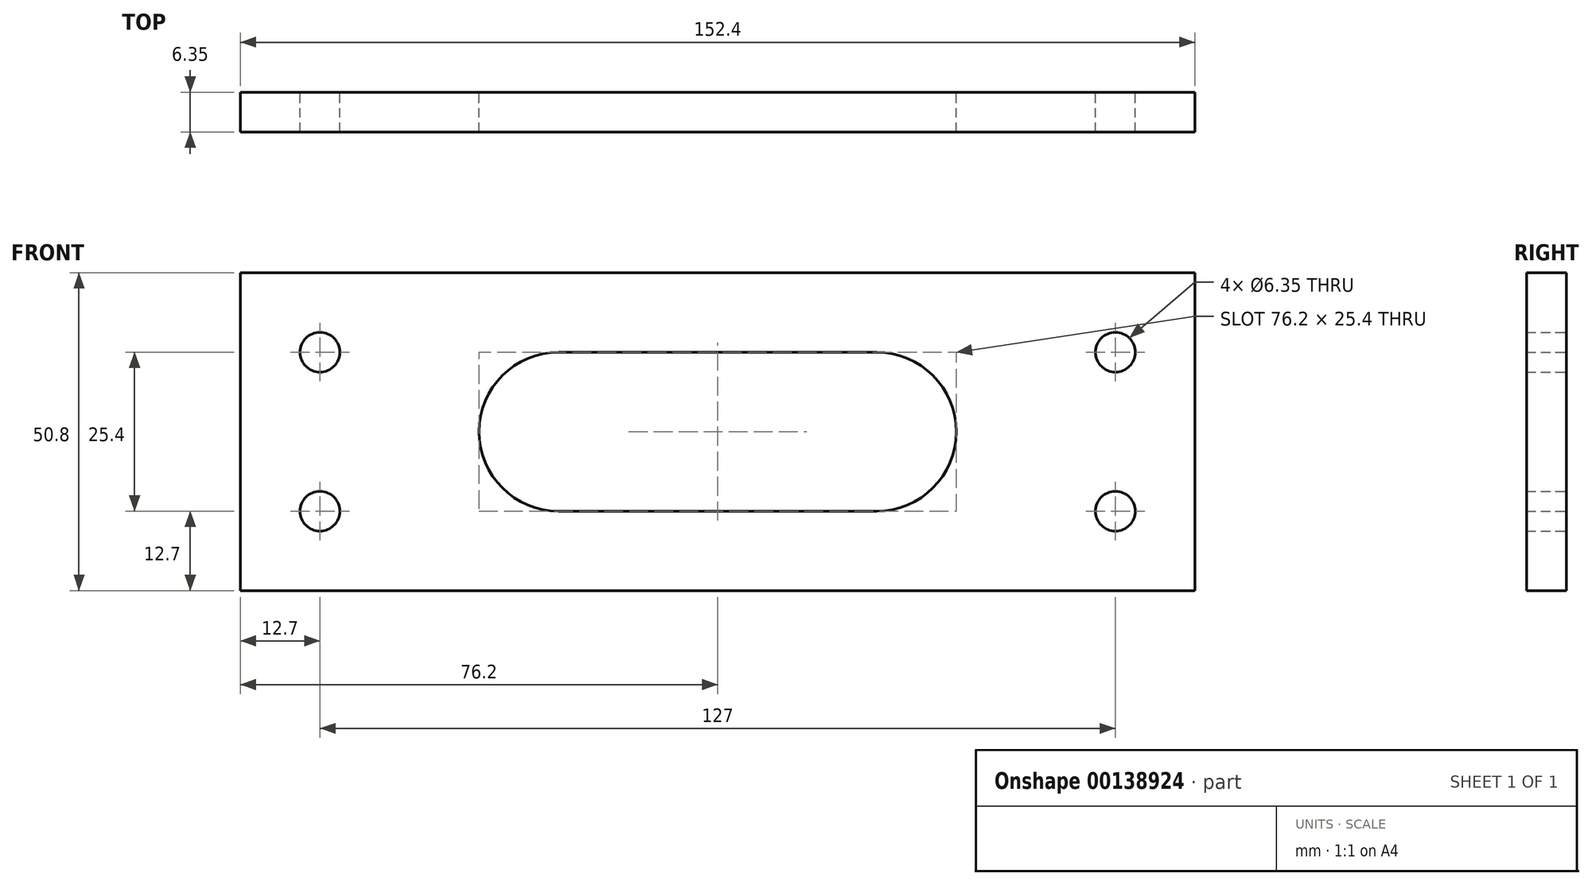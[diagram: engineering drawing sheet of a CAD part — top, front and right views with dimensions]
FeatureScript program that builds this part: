
annotation { "Feature Type Name" : "Feature", "Feature Type Description" : "" }
export const myFeature = defineFeature(function(context is Context, id is Id, definition is map)
    precondition{}
    {
        {
            var Q0;
            Q0=qCreatedBy(makeId("Front.planeOp"),FACE);
            var sketch = newSketch(context, id + "F0", { "sketchPlane" : qUnion([Q0])});
            skLineSegment(sketch, "E0.bottom", {"start": v(-76.2, 25.4) * mm, "end": v(76.2, 25.4) * mm});
            skLineSegment(sketch, "E0.top", {"start": v(-76.2, -25.4) * mm, "end": v(76.2, -25.4) * mm});
            skLineSegment(sketch, "E0.left", {"start": v(-76.2, 25.4) * mm, "end": v(-76.2, -25.4) * mm});
            skLineSegment(sketch, "E0.right", {"start": v(76.2, 25.4) * mm, "end": v(76.2, -25.4) * mm});
            skPoint(sketch, "E0.middle", {"position": v(0, 0) * mm});
            skCircle(sketch, "E1", {"center": v(-63.5, 12.7) * mm, "radius": 3.18 * mm});
            skLineSegment(sketch, "E2", {"start": v(-76.2, 0) * mm, "end": v(76.2, 0) * mm, "construction": true});
            skCircle(sketch, "E3.MirrorC", {"center": v(-63.5, -12.7) * mm, "radius": 3.18 * mm});
            skLineSegment(sketch, "E4", {"start": v(0, 25.4) * mm, "end": v(0, -25.4) * mm, "construction": true});
            skCircle(sketch, "E5.MirrorC", {"center": v(63.5, 12.7) * mm, "radius": 3.18 * mm});
            skCircle(sketch, "E6.MirrorC", {"center": v(63.5, -12.7) * mm, "radius": 3.18 * mm});
            skArc(sketch, "E7", {"start": v(-25.4, -12.7) * mm, "mid": v(-38.1, 0) * mm, "end": v(-25.4, 12.7) * mm});
            skArc(sketch, "E8.MirrorCS", {"start": v(25.4, -12.7) * mm, "mid": v(38.1, 0) * mm, "end": v(25.4, 12.7) * mm});
            skLineSegment(sketch, "E9", {"start": v(-25.4, 12.7) * mm, "end": v(25.4, 12.7) * mm});
            skLineSegment(sketch, "E10", {"start": v(-25.4, -12.7) * mm, "end": v(25.4, -12.7) * mm});
            skSolve(sketch);
        }
        {
            var Q0;
            Q0=makeQuery(id+"F0.imprint","IMPRINT",FACE,{"disambiguationData":[TD([[makeQuery(id+"F0.imprint","IMPRINT",EDGE,{"derivedFrom":sQuery(id+"F0.wireOp",EDGE,"E0.bottom")}),-1.0]])]});
            extrude(context, id + "F1", {"entities" : qUnion([Q0]), "depth" : 6.35 * mm});
        }
    });
